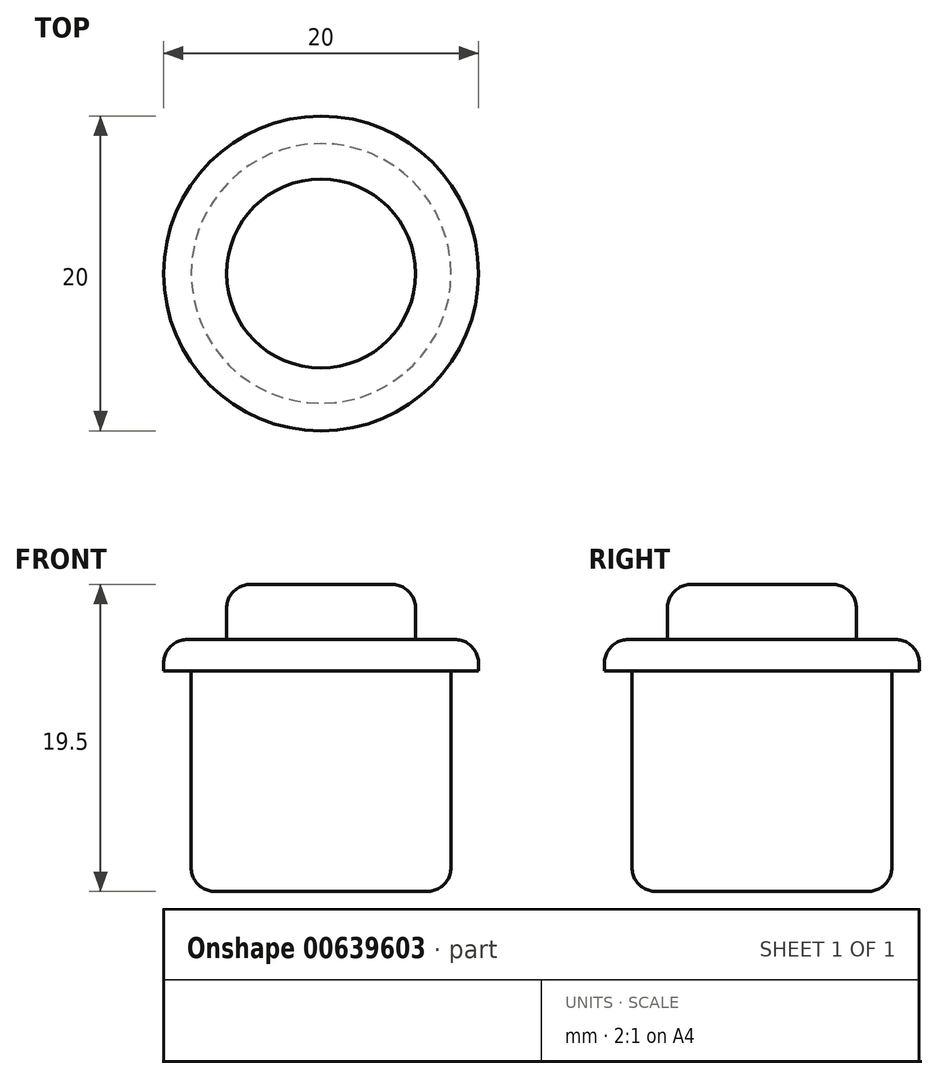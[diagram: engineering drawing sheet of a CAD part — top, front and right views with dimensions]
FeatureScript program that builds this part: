
annotation { "Feature Type Name" : "Feature", "Feature Type Description" : "" }
export const myFeature = defineFeature(function(context is Context, id is Id, definition is map)
    precondition{}
    {
        {
            var Q0;
            Q0=qCreatedBy(makeId("Top.planeOp"),FACE);
            var sketch = newSketch(context, id + "F0", { "sketchPlane" : qUnion([Q0])});
            skCircle(sketch, "E0", {"center": v(0, 0) * mm, "radius": 10 * mm});
            skCircle(sketch, "E1", {"center": v(0, 0) * mm, "radius": 8.25 * mm});
            skCircle(sketch, "E2", {"center": v(0, 0) * mm, "radius": 6 * mm});
            skSolve(sketch);
        }
        {
            var Q0;
            Q0=makeQuery(id+"F0.imprint","IMPRINT",FACE,{"disambiguationData":[TD([[makeQuery(id+"F0.imprint","IMPRINT",EDGE,{"derivedFrom":sQuery(id+"F0.wireOp",EDGE,"E2")}),1.0]])]});
            extrude(context, id + "F1", {"entities" : qUnion([Q0]), "depth" : 5.5 * mm, "offsetDistance" : 25 * mm});
        }
        {
            var Q0;
            Q0=makeQuery(id+"F0.imprint","IMPRINT",FACE,{"disambiguationData":[TD([[makeQuery(id+"F0.imprint","IMPRINT",EDGE,{"derivedFrom":sQuery(id+"F0.wireOp",EDGE,"E1")}),1.0]])]});
            var Q1;
            Q1=makeQuery(id+"F0.imprint","IMPRINT",FACE,{"disambiguationData":[TD([[makeQuery(id+"F0.imprint","IMPRINT",EDGE,{"derivedFrom":sQuery(id+"F0.wireOp",EDGE,"E0")}),1.0]])]});
            extrude(context, id + "F2", {"entities" : qUnion([Q0, Q1]), "operationType" : NewBodyOperationType.ADD, "depth" : 2 * mm, "offsetDistance" : 25 * mm});
        }
        {
            var Q0;
            Q0=makeQuery(id+"F0.imprint","IMPRINT",FACE,{"disambiguationData":[TD([[makeQuery(id+"F0.imprint","IMPRINT",EDGE,{"derivedFrom":sQuery(id+"F0.wireOp",EDGE,"E1")}),1.0]])]});
            var Q1;
            Q1=makeQuery(id+"F0.imprint","IMPRINT",FACE,{"disambiguationData":[TD([[makeQuery(id+"F0.imprint","IMPRINT",EDGE,{"derivedFrom":sQuery(id+"F0.wireOp",EDGE,"E2")}),1.0]])]});
            extrude(context, id + "F3", {"entities" : qUnion([Q0, Q1]), "operationType" : NewBodyOperationType.ADD, "oppositeDirection" : true, "depth" : 14 * mm, "offsetDistance" : 25 * mm});
        }
        {
            var Q0;
            Q0=makeQuery(id+"F2.opExtrude","CAP_EDGE",EDGE,{"disambiguationData":[OSD([sQuery(id+"F0.wireOp",EDGE,"E0")])],"isStart":false});
            var Q1;
            Q1=makeQuery(id+"F1.opExtrude","CAP_EDGE",EDGE,{"disambiguationData":[OSD([sQuery(id+"F0.wireOp",EDGE,"E2")])],"isStart":false});
            var Q2;
            Q2=makeQuery(id+"F3.opExtrude","CAP_EDGE",EDGE,{"disambiguationData":[OSD([sQuery(id+"F0.wireOp",EDGE,"E1")])],"isStart":false});
            fillet(context, id + "F4", {"entities" : qUnion([Q0, Q1, Q2]), "radius" : 1.5 * mm, "tangentPropagation" : true, "allowEdgeOverflow" : false});
        }
    });
